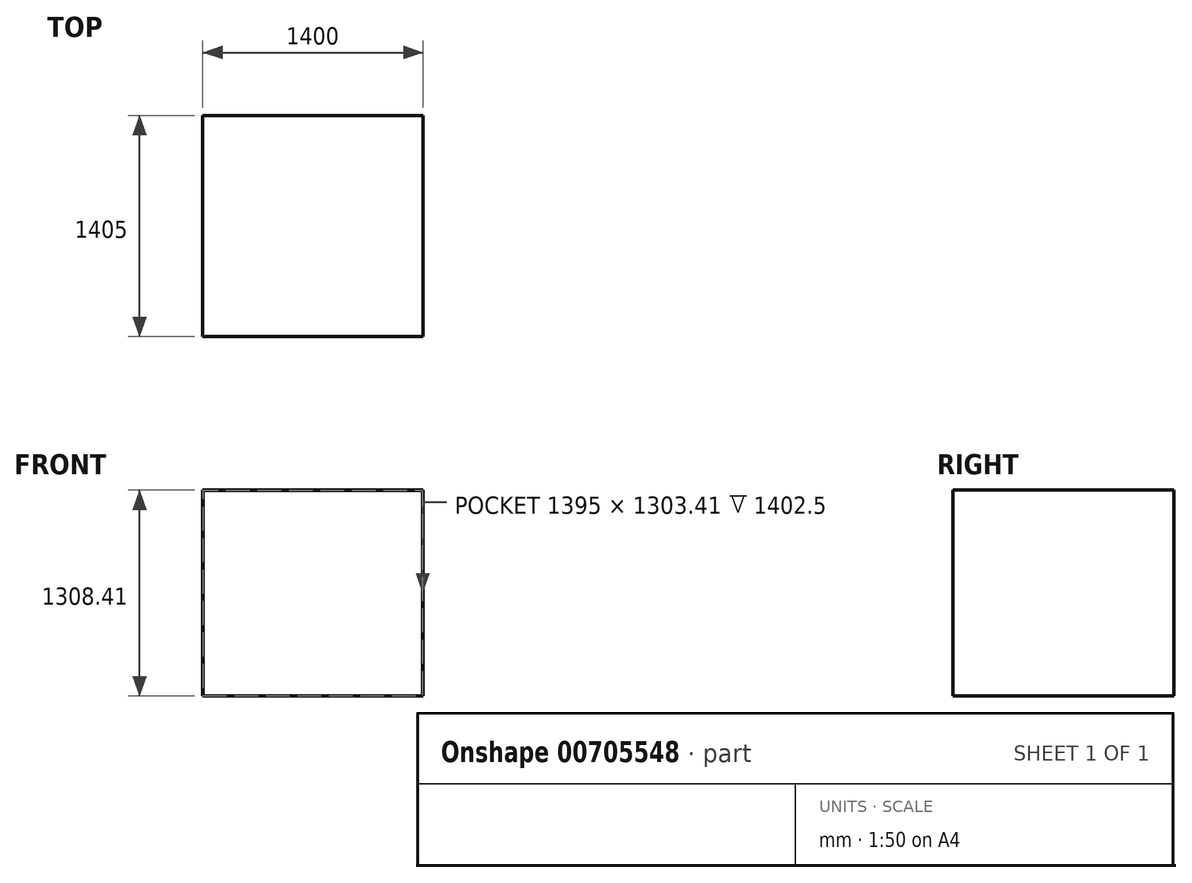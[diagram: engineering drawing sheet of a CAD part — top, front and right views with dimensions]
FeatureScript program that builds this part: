
annotation { "Feature Type Name" : "Feature", "Feature Type Description" : "" }
export const myFeature = defineFeature(function(context is Context, id is Id, definition is map)
    precondition{}
    {
        {
            var Q0;
            Q0=qCreatedBy(makeId("Front.planeOp"),FACE);
            var sketch = newSketch(context, id + "F0", { "sketchPlane" : qUnion([Q0])});
            skLineSegment(sketch, "E0.bottom", {"start": v(-730.78, 675.83) * mm, "end": v(669.22, 675.83) * mm});
            skLineSegment(sketch, "E0.top", {"start": v(-730.78, -632.58) * mm, "end": v(669.22, -632.58) * mm});
            skLineSegment(sketch, "E0.left", {"start": v(-730.78, 675.83) * mm, "end": v(-730.78, -632.58) * mm});
            skLineSegment(sketch, "E0.right", {"start": v(669.22, 675.83) * mm, "end": v(669.22, -632.58) * mm});
            skSolve(sketch);
        }
        {
            var Q0;
            Q0=makeQuery(id+"F0.imprint","IMPRINT",FACE,{"disambiguationData":[TD([[makeQuery(id+"F0.imprint","IMPRINT",EDGE,{"derivedFrom":sQuery(id+"F0.wireOp",EDGE,"E0.bottom")}),-1.0]])]});
            extrude(context, id + "F1", {"entities" : qUnion([Q0]), "depth" : 20 * mm, "offsetDistance" : 25 * mm});
        }
        {
            var Q0;
            Q0=makeQuery(id+"F1.opExtrude","CAP_FACE",FACE,{"disambiguationData":[OSD([sQuery(id+"F0.wireOp",EDGE,"E0.bottom"),sQuery(id+"F0.wireOp",EDGE,"E0.top"),sQuery(id+"F0.wireOp",EDGE,"E0.left"),sQuery(id+"F0.wireOp",EDGE,"E0.right")])],"isStart":false});
            var Q1;
            Q1=makeQuery(id+"F1.opExtrude","CAP_FACE",FACE,{"disambiguationData":[OSD([sQuery(id+"F0.wireOp",EDGE,"E0.bottom"),sQuery(id+"F0.wireOp",EDGE,"E0.top"),sQuery(id+"F0.wireOp",EDGE,"E0.left"),sQuery(id+"F0.wireOp",EDGE,"E0.right")])],"isStart":true});
            extrude(context, id + "F2", {"entities" : qUnion([Q0, Q1]), "operationType" : NewBodyOperationType.ADD, "oppositeDirection" : true, "depth" : 1385 * mm, "offsetDistance" : 25 * mm});
        }
        {
            var Q0;
            Q0=makeQuery(id+"F1.opExtrude","CAP_FACE",FACE,{"disambiguationData":[OSD([sQuery(id+"F0.wireOp",EDGE,"E0.bottom"),sQuery(id+"F0.wireOp",EDGE,"E0.top"),sQuery(id+"F0.wireOp",EDGE,"E0.left"),sQuery(id+"F0.wireOp",EDGE,"E0.right")])],"isStart":false});
            shell(context, id + "F3", {"entities" : qUnion([Q0]), "thickness" : 2.5 * mm});
        }
    });
